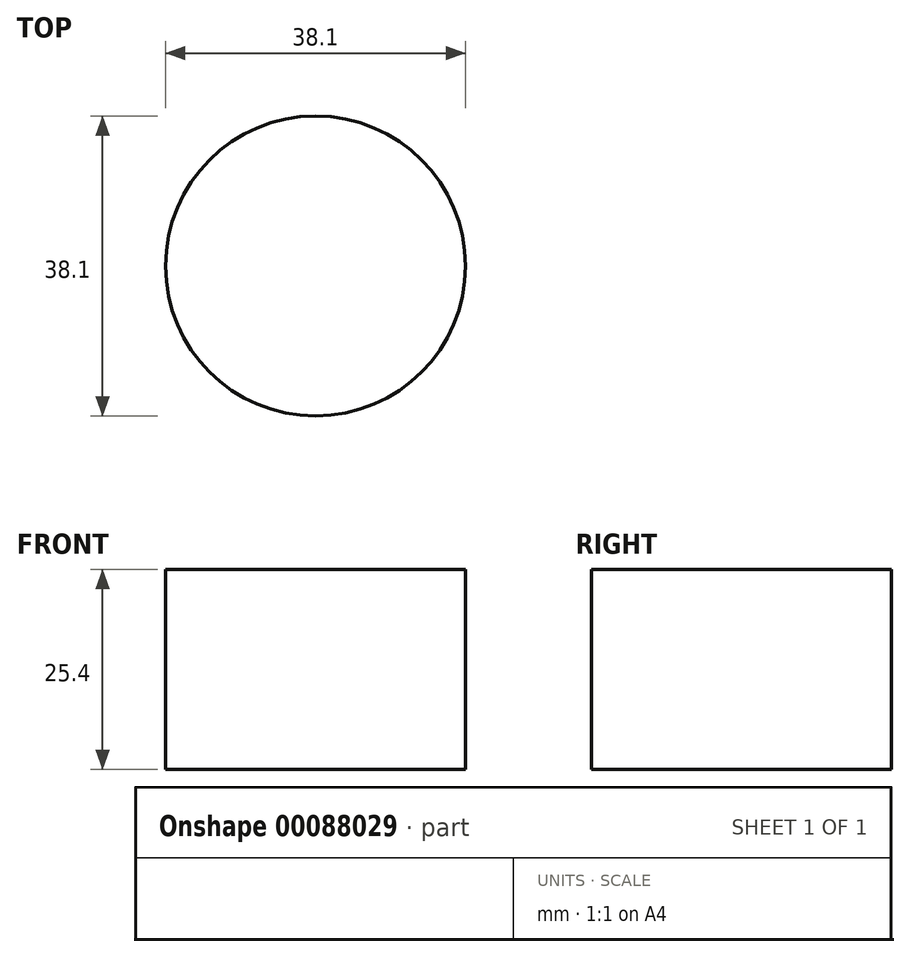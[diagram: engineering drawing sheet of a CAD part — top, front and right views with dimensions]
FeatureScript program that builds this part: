
annotation { "Feature Type Name" : "Feature", "Feature Type Description" : "" }
export const myFeature = defineFeature(function(context is Context, id is Id, definition is map)
    precondition{}
    {
        {
            var Q0;
            Q0=qCreatedBy(makeId("Top.planeOp"),FACE);
            var sketch = newSketch(context, id + "F0", { "sketchPlane" : qUnion([Q0])});
            skCircle(sketch, "E0", {"center": v(0, 0) * mm, "radius": 19.05 * mm});
            skSolve(sketch);
        }
        {
            var Q0;
            Q0=makeQuery(id+"F0.imprint","IMPRINT",FACE,{"disambiguationData":[TD([[makeQuery(id+"F0.imprint","IMPRINT",EDGE,{"derivedFrom":sQuery(id+"F0.wireOp",EDGE,"E0")}),1.0]])]});
            extrude(context, id + "F1", {"entities" : qUnion([Q0]), "depth" : 25.4 * mm});
        }
    });
